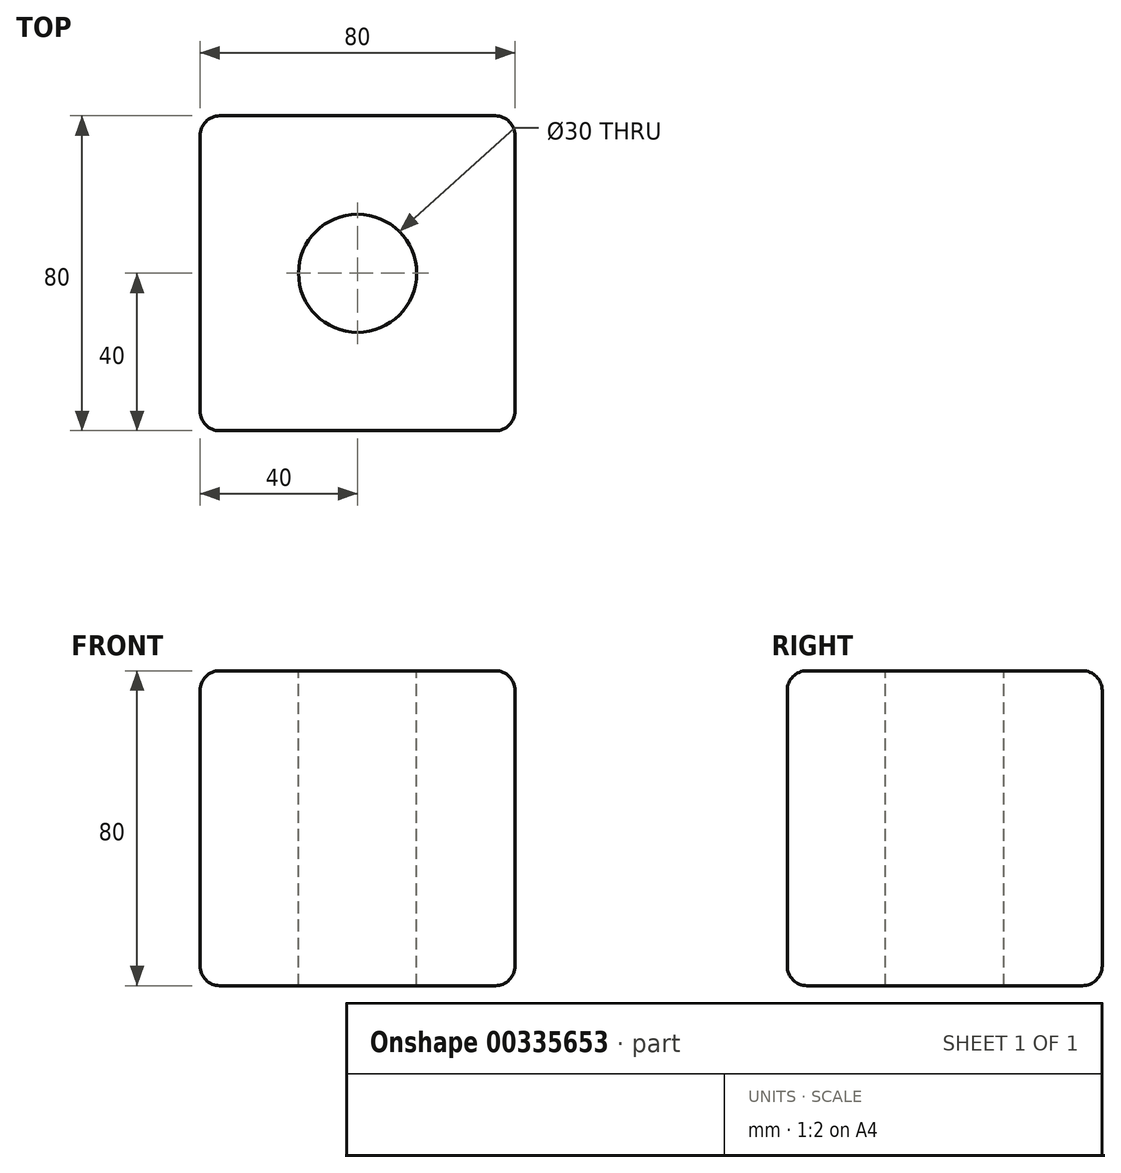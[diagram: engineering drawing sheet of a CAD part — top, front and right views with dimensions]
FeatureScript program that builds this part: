
annotation { "Feature Type Name" : "Feature", "Feature Type Description" : "" }
export const myFeature = defineFeature(function(context is Context, id is Id, definition is map)
    precondition{}
    {
        {
            var Q0;
            Q0=qCreatedBy(makeId("Top.planeOp"),FACE);
            var sketch = newSketch(context, id + "F0", { "sketchPlane" : qUnion([Q0])});
            skLineSegment(sketch, "E0.bottom", {"start": v(40, -40) * mm, "end": v(-40, -40) * mm});
            skLineSegment(sketch, "E0.top", {"start": v(40, 40) * mm, "end": v(-40, 40) * mm});
            skLineSegment(sketch, "E0.left", {"start": v(40, -40) * mm, "end": v(40, 40) * mm});
            skLineSegment(sketch, "E0.right", {"start": v(-40, -40) * mm, "end": v(-40, 40) * mm});
            skPoint(sketch, "E0.middle", {"position": v(0, 0) * mm});
            skSolve(sketch);
        }
        {
            var Q0;
            Q0=makeQuery(id+"F0.imprint","IMPRINT",FACE,{"disambiguationData":[TD([[makeQuery(id+"F0.imprint","IMPRINT",EDGE,{"derivedFrom":sQuery(id+"F0.wireOp",EDGE,"E0.bottom")}),-1.0]])]});
            extrude(context, id + "F1", {"entities" : qUnion([Q0]), "endBound" : BoundingType.SYMMETRIC, "depth" : 80 * mm});
        }
        {
            var Q0;
            Q0=makeQuery(id+"F1.opExtrude","CAP_EDGE",EDGE,{"disambiguationData":[OSD([sQuery(id+"F0.wireOp",EDGE,"E0.top")])],"isStart":false});
            var Q1;
            Q1=makeQuery(id+"F1.opExtrude","CAP_EDGE",EDGE,{"disambiguationData":[OSD([sQuery(id+"F0.wireOp",EDGE,"E0.bottom")])],"isStart":false});
            var Q2;
            Q2=makeQuery(id+"F1.opExtrude","CAP_EDGE",EDGE,{"disambiguationData":[OSD([sQuery(id+"F0.wireOp",EDGE,"E0.left")])],"isStart":false});
            var Q3;
            Q3=makeQuery(id+"F1.opExtrude","SWEPT_EDGE",EDGE,{"disambiguationData":[OSD([sQuery(id+"F0.wireOp",EDGE,"E0.top"),sQuery(id+"F0.wireOp",EDGE,"E0.right")])]});
            var Q4;
            Q4=makeQuery(id+"F1.opExtrude","CAP_EDGE",EDGE,{"disambiguationData":[OSD([sQuery(id+"F0.wireOp",EDGE,"E0.right")])],"isStart":true});
            var Q5;
            Q5=makeQuery(id+"F1.opExtrude","SWEPT_EDGE",EDGE,{"disambiguationData":[OSD([sQuery(id+"F0.wireOp",EDGE,"E0.bottom"),sQuery(id+"F0.wireOp",EDGE,"E0.right")])]});
            var Q6;
            Q6=makeQuery(id+"F1.opExtrude","CAP_EDGE",EDGE,{"disambiguationData":[OSD([sQuery(id+"F0.wireOp",EDGE,"E0.right")])],"isStart":false});
            var Q7;
            Q7=makeQuery(id+"F1.opExtrude","SWEPT_EDGE",EDGE,{"disambiguationData":[OSD([sQuery(id+"F0.wireOp",EDGE,"E0.top"),sQuery(id+"F0.wireOp",EDGE,"E0.left")])]});
            var Q8;
            Q8=makeQuery(id+"F1.opExtrude","CAP_EDGE",EDGE,{"disambiguationData":[OSD([sQuery(id+"F0.wireOp",EDGE,"E0.left")])],"isStart":true});
            var Q9;
            Q9=makeQuery(id+"F1.opExtrude","SWEPT_EDGE",EDGE,{"disambiguationData":[OSD([sQuery(id+"F0.wireOp",EDGE,"E0.bottom"),sQuery(id+"F0.wireOp",EDGE,"E0.left")])]});
            var Q10;
            Q10=makeQuery(id+"F1.opExtrude","CAP_EDGE",EDGE,{"disambiguationData":[OSD([sQuery(id+"F0.wireOp",EDGE,"E0.bottom")])],"isStart":true});
            fillet(context, id + "F2", {"entities" : qUnion([Q0, Q1, Q2, Q3, Q4, Q5, Q6, Q7, Q8, Q9, Q10]), "radius" : 5 * mm, "tangentPropagation" : true, "allowEdgeOverflow" : false});
        }
        {
            var Q0;
            Q0=makeQuery(id+"F1.opExtrude","CAP_EDGE",EDGE,{"disambiguationData":[OSD([sQuery(id+"F0.wireOp",EDGE,"E0.top")])],"isStart":true});
            fillet(context, id + "F3", {"entities" : qUnion([Q0]), "radius" : 5 * mm, "tangentPropagation" : true, "allowEdgeOverflow" : false});
        }
        {
            var Q0;
            Q0=makeQuery(id+"F1.opExtrude","CAP_FACE",FACE,{"disambiguationData":[OSD([sQuery(id+"F0.wireOp",EDGE,"E0.bottom"),sQuery(id+"F0.wireOp",EDGE,"E0.top"),sQuery(id+"F0.wireOp",EDGE,"E0.left"),sQuery(id+"F0.wireOp",EDGE,"E0.right")])],"isStart":false});
            var sketch = newSketch(context, id + "F4", { "sketchPlane" : qUnion([Q0])});
            skCircle(sketch, "E1", {"center": v(0, 0) * mm, "radius": 15 * mm});
            skSolve(sketch);
        }
        {
            var Q0;
            Q0=makeQuery(id+"F4.imprint","IMPRINT",FACE,{"disambiguationData":[TD([[makeQuery(id+"F4.imprint","IMPRINT",EDGE,{"derivedFrom":sQuery(id+"F4.wireOp",EDGE,"E1")}),1.0]])]});
            extrude(context, id + "F5", {"entities" : qUnion([Q0]), "operationType" : NewBodyOperationType.REMOVE, "endBound" : BoundingType.THROUGH_ALL, "oppositeDirection" : true, "depth" : 25 * mm});
        }
    });
